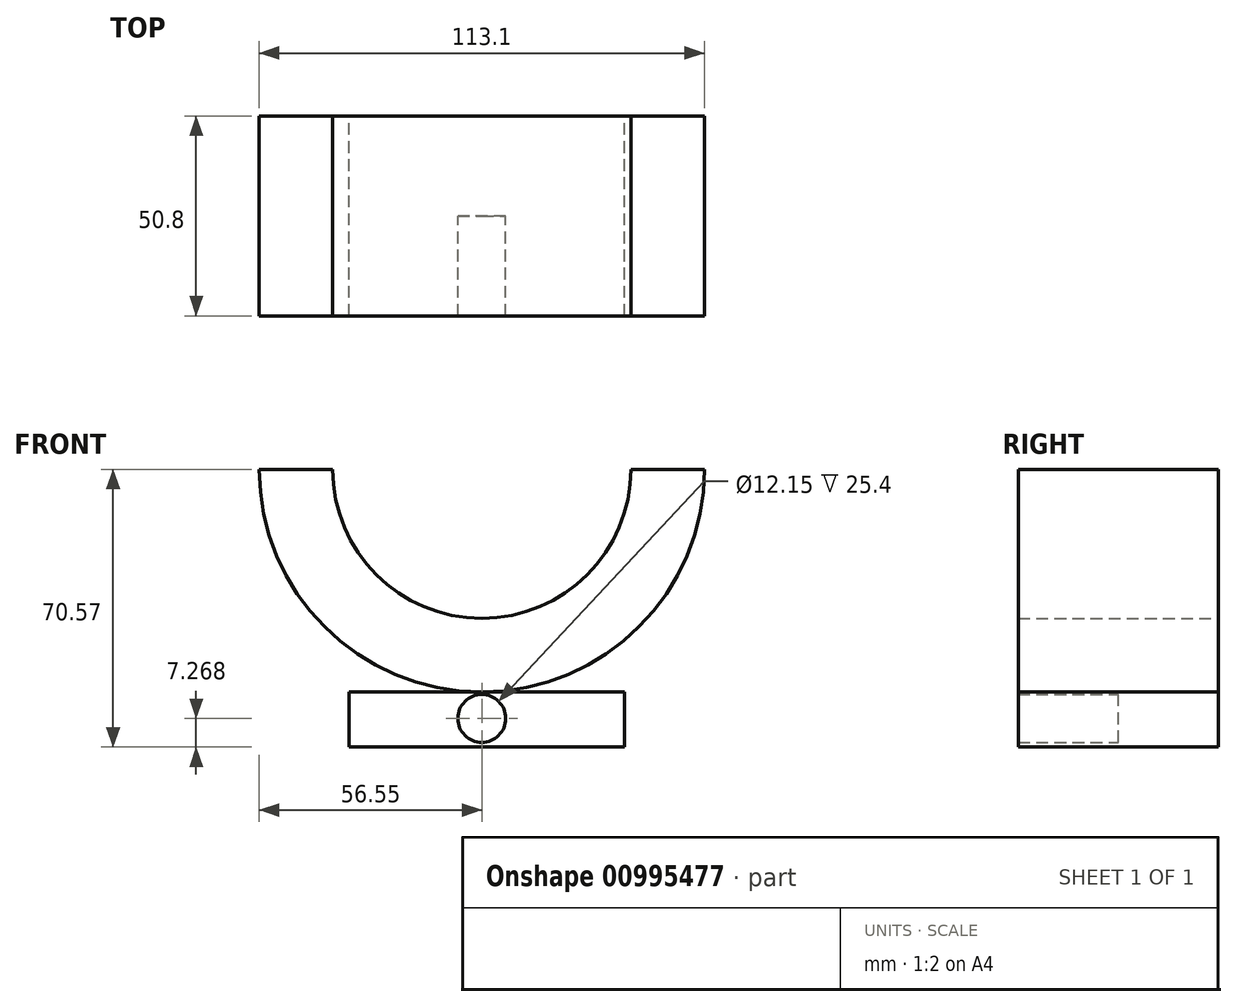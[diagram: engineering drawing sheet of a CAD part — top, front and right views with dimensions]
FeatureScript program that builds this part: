
annotation { "Feature Type Name" : "Feature", "Feature Type Description" : "" }
export const myFeature = defineFeature(function(context is Context, id is Id, definition is map)
    precondition{}
    {
        {
            var Q0;
            Q0=qCreatedBy(makeId("Front.planeOp"),FACE);
            var sketch = newSketch(context, id + "F0", { "sketchPlane" : qUnion([Q0])});
            skArc(sketch, "E0", {"start": v(-56.55, 0) * mm, "mid": v(0, -56.55) * mm, "end": v(56.55, 0) * mm});
            skArc(sketch, "E1", {"start": v(-37.88, 0) * mm, "mid": v(0, -37.88) * mm, "end": v(37.88, 0) * mm});
            skLineSegment(sketch, "E2", {"start": v(37.88, 0) * mm, "end": v(56.55, 0) * mm});
            skLineSegment(sketch, "E3", {"start": v(56.55, 0) * mm, "end": v(37.88, 0) * mm});
            skLineSegment(sketch, "E4", {"start": v(-37.88, 0) * mm, "end": v(-56.55, 0) * mm});
            skLineSegment(sketch, "E5", {"start": v(0, -56.55) * mm, "end": v(-33.7, -56.55) * mm});
            skLineSegment(sketch, "E6", {"start": v(-33.7, -56.55) * mm, "end": v(-33.7, -70.57) * mm});
            skLineSegment(sketch, "E7", {"start": v(-33.7, -70.57) * mm, "end": v(36.21, -70.57) * mm});
            skLineSegment(sketch, "E8", {"start": v(36.21, -70.57) * mm, "end": v(36.21, -56.55) * mm});
            skLineSegment(sketch, "E9", {"start": v(36.21, -56.55) * mm, "end": v(0, -56.55) * mm});
            skSolve(sketch);
        }
        {
            var Q0;
            Q0=qCreatedBy(makeId("Front.planeOp"),FACE);
            var sketch = newSketch(context, id + "F1", { "sketchPlane" : qUnion([Q0])});
            skCircle(sketch, "E10", {"center": v(0, -63.3) * mm, "radius": 6.07 * mm});
            skSolve(sketch);
        }
        {
            var Q0;
            Q0 = qSketchRegion(id + "F0", true);
            extrude(context, id + "F2", {"entities" : qUnion([Q0]), "endBound" : BoundingType.SYMMETRIC, "depth" : 50.8 * mm, "offsetDistance" : 25.4 * mm});
        }
        {
            var Q0;
            Q0 = qSketchRegion(id + "F1", true);
            extrude(context, id + "F3", {"entities" : qUnion([Q0]), "operationType" : NewBodyOperationType.REMOVE, "depth" : 134.88 * mm, "offsetDistance" : 25.4 * mm});
        }
    });
